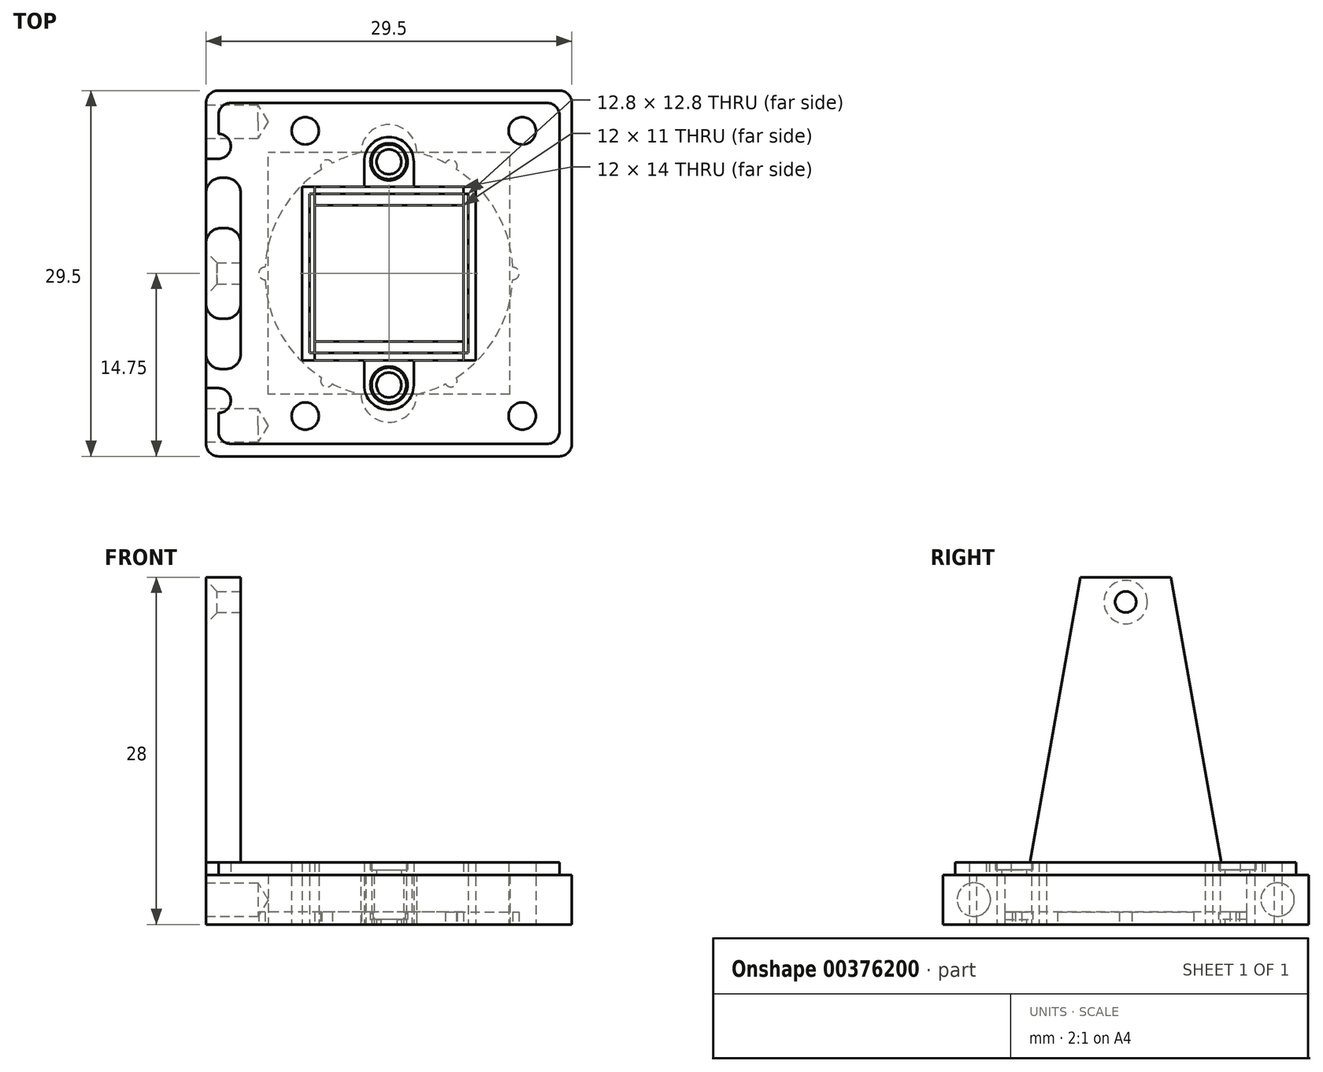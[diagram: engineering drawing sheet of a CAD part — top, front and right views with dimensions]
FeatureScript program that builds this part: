
annotation { "Feature Type Name" : "Feature", "Feature Type Description" : "" }
export const myFeature = defineFeature(function(context is Context, id is Id, definition is map)
    precondition{}
    {
        {
            var Q0;
            Q0=qCreatedBy(makeId("Top.planeOp"),FACE);
            var sketch = newSketch(context, id + "F0", { "sketchPlane" : qUnion([Q0])});
            skLineSegment(sketch, "E0.bottom", {"start": v(14.75, -14.75) * mm, "end": v(-14.75, -14.75) * mm});
            skLineSegment(sketch, "E0.top", {"start": v(14.75, 14.75) * mm, "end": v(-14.75, 14.75) * mm});
            skLineSegment(sketch, "E0.left", {"start": v(14.75, -14.75) * mm, "end": v(14.75, 14.75) * mm});
            skLineSegment(sketch, "E0.right", {"start": v(-14.75, -14.75) * mm, "end": v(-14.75, 14.75) * mm});
            skPoint(sketch, "E0.middle", {"position": v(0, 0) * mm});
            skLineSegment(sketch, "E1.0", {"start": v(-9.75, -9.75) * mm, "end": v(-9.75, 9.75) * mm});
            skLineSegment(sketch, "E1.1", {"start": v(9.75, -9.75) * mm, "end": v(-9.75, -9.75) * mm});
            skLineSegment(sketch, "E1.2", {"start": v(9.75, -9.75) * mm, "end": v(9.75, 9.75) * mm});
            skLineSegment(sketch, "E1.3", {"start": v(9.75, 9.75) * mm, "end": v(-9.75, 9.75) * mm});
            skSolve(sketch);
        }
        {
            var Q0;
            Q0 = qSketchRegion(id + "F0", true);
            extrude(context, id + "F1", {"entities" : qUnion([Q0]), "depth" : 4 * mm, "offsetDistance" : 25 * mm});
        }
        {
            var Q0;
            Q0=makeQuery(id+"F1.opExtrude","CAP_FACE",FACE,{"disambiguationData":[OSD([sQuery(id+"F0.wireOp",EDGE,"E0.bottom"),sQuery(id+"F0.wireOp",EDGE,"E0.top"),sQuery(id+"F0.wireOp",EDGE,"E0.left"),sQuery(id+"F0.wireOp",EDGE,"E0.right"),sQuery(id+"F0.wireOp",EDGE,"E1.0"),sQuery(id+"F0.wireOp",EDGE,"E1.1"),sQuery(id+"F0.wireOp",EDGE,"E1.2"),sQuery(id+"F0.wireOp",EDGE,"E1.3")])],"isStart":false});
            var sketch = newSketch(context, id + "F2", { "sketchPlane" : qUnion([Q0])});
            skLineSegment(sketch, "E2.0", {"start": v(13.75, 13.75) * mm, "end": v(-13.75, 13.75) * mm});
            skLineSegment(sketch, "E2.1", {"start": v(13.75, -13.75) * mm, "end": v(13.75, 13.75) * mm});
            skLineSegment(sketch, "E2.2", {"start": v(13.75, -13.75) * mm, "end": v(-13.75, -13.75) * mm});
            skLineSegment(sketch, "E2.3", {"start": v(-13.75, -13.75) * mm, "end": v(-13.75, -11.25) * mm});
            skLineSegment(sketch, "E3.bottom", {"start": v(-14.75, -8.65) * mm, "end": v(-11.95, -8.65) * mm});
            skLineSegment(sketch, "E3.top", {"start": v(-14.75, 8.65) * mm, "end": v(-11.95, 8.65) * mm});
            skLineSegment(sketch, "E3.left", {"start": v(-14.75, -8.65) * mm, "end": v(-14.75, 8.65) * mm});
            skLineSegment(sketch, "E3.right", {"start": v(-11.95, -8.65) * mm, "end": v(-11.95, 8.65) * mm});
            skPoint(sketch, "E3.middle", {"position": v(-13.35, 0) * mm});
            skPoint(sketch, "E3.middle.positionSnap0", {"position": v(-13.75, 0) * mm});
            skPoint(sketch, "E3.centerSnap0", {"position": v(-13.75, 0) * mm});
            skLineSegment(sketch, "E4.trimOffspring", {"start": v(-13.75, 11.25) * mm, "end": v(-13.75, 13.75) * mm});
            skArc(sketch, "E5", {"start": v(-13.75, 9.25) * mm, "mid": v(-12.75, 10.25) * mm, "end": v(-13.75, 11.25) * mm});
            skArc(sketch, "E6", {"start": v(-13.75, -11.25) * mm, "mid": v(-12.75, -10.25) * mm, "end": v(-13.75, -9.25) * mm});
            skLineSegment(sketch, "E7", {"start": v(-13.75, -9.25) * mm, "end": v(-14.75, -9.25) * mm});
            skLineSegment(sketch, "E8", {"start": v(-13.75, 9.25) * mm, "end": v(-14.75, 9.25) * mm});
            skCircle(sketch, "E9", {"center": v(0, 9.75) * mm, "radius": 2.25 * mm});
            skCircle(sketch, "E10", {"center": v(0, -9.75) * mm, "radius": 2.25 * mm});
            skCircle(sketch, "E11", {"center": v(0, 9.75) * mm, "radius": 1.25 * mm, "construction": true});
            skCircle(sketch, "E12", {"center": v(0, -9.75) * mm, "radius": 1.25 * mm, "construction": true});
            skLineSegment(sketch, "E13", {"start": v(-13.35, 0) * mm, "end": v(0, 0) * mm, "construction": true});
            skLineSegment(sketch, "E14.bottom", {"start": v(6, -7) * mm, "end": v(-6, -7) * mm});
            skLineSegment(sketch, "E14.top", {"start": v(6, 7) * mm, "end": v(-6, 7) * mm});
            skLineSegment(sketch, "E14.left", {"start": v(6, -7) * mm, "end": v(6, 7) * mm});
            skLineSegment(sketch, "E14.right", {"start": v(-6, -7) * mm, "end": v(-6, 7) * mm});
            skPoint(sketch, "E14.middle", {"position": v(0, 0) * mm});
            skSolve(sketch);
        }
        {
            var Q0;
            {var subQ5=sQuery(id+"F2.wireOp",EDGE,"E3.left");Q0=makeQuery(id+"F2.imprint","IMPRINT",FACE,{"disambiguationData":[TD([[makeQuery(id+"F2.imprint","IMPRINT",EDGE,{"derivedFrom":subQ5}),-1.0]])]});}
            var Q1;
            {var subQ5=sQuery(id+"F2.wireOp",EDGE,"E3.right");Q1=makeQuery(id+"F2.imprint","IMPRINT",FACE,{"disambiguationData":[TD([[makeQuery(id+"F2.imprint","IMPRINT",EDGE,{"derivedFrom":subQ5}),1.0]])]});}
            extrude(context, id + "F3", {"entities" : qUnion([Q0, Q1]), "operationType" : NewBodyOperationType.ADD, "depth" : 24 * mm, "offsetDistance" : 25 * mm});
        }
        {
            var Q0;
            Q0=makeQuery(id+"F3.opExtrude","CAP_EDGE",EDGE,{"disambiguationData":[OSD([sQuery(id+"F2.wireOp",EDGE,"E3.bottom")])],"isStart":false});
            var Q1;
            Q1=makeQuery(id+"F3.opExtrude","CAP_EDGE",EDGE,{"disambiguationData":[OSD([sQuery(id+"F2.wireOp",EDGE,"E3.top")])],"isStart":false});
            chamfer(context, id + "F4", {"entities" : qUnion([Q0, Q1]), "chamferType" : ChamferType.OFFSET_ANGLE, "width" : 5 * mm, "oppositeDirection" : false, "angle" : 80 * degree, "tangentPropagation" : true});
        }
        {
            var Q0;
            Q0=makeQuery(id+"F4.opChamfer","BLEND_EDGE",EDGE,{"blendedFrom":[makeQuery(id+"F3.opExtrude","CAP_EDGE",EDGE,{"disambiguationData":[OSD([sQuery(id+"F2.wireOp",EDGE,"E3.bottom")])],"isStart":false}),makeQuery(id+"F3.opExtrude","SWEPT_FACE",FACE,{"disambiguationData":[OSD([sQuery(id+"F2.wireOp",EDGE,"E3.right")])]})],"blendedInto":[makeQuery(id+"F3.opExtrude","SWEPT_FACE",FACE,{"disambiguationData":[OSD([sQuery(id+"F2.wireOp",EDGE,"E3.right")])]})]});
            var Q1;
            Q1=makeQuery(id+"F4.opChamfer","BLEND_EDGE",EDGE,{"blendedFrom":[makeQuery(id+"F3.opExtrude","CAP_EDGE",EDGE,{"disambiguationData":[OSD([sQuery(id+"F2.wireOp",EDGE,"E3.bottom")])],"isStart":false}),makeQuery(id+"F3.boolean.opBoolean","MERGE",FACE,{"derivedFrom":[makeQuery(id+"F1.opExtrude","SWEPT_FACE",FACE,{"disambiguationData":[OSD([sQuery(id+"F0.wireOp",EDGE,"E0.right")])]}),makeQuery(id+"F3.opExtrude","SWEPT_FACE",FACE,{"disambiguationData":[OSD([sQuery(id+"F2.wireOp",EDGE,"E3.left")])]})]})],"blendedInto":[makeQuery(id+"F3.boolean.opBoolean","MERGE",FACE,{"derivedFrom":[makeQuery(id+"F1.opExtrude","SWEPT_FACE",FACE,{"disambiguationData":[OSD([sQuery(id+"F0.wireOp",EDGE,"E0.right")])]}),makeQuery(id+"F3.opExtrude","SWEPT_FACE",FACE,{"disambiguationData":[OSD([sQuery(id+"F2.wireOp",EDGE,"E3.left")])]})]})]});
            var Q2;
            Q2=makeQuery(id+"F4.opChamfer","BLEND_EDGE",EDGE,{"blendedFrom":[makeQuery(id+"F3.opExtrude","CAP_EDGE",EDGE,{"disambiguationData":[OSD([sQuery(id+"F2.wireOp",EDGE,"E3.top")])],"isStart":false}),makeQuery(id+"F3.opExtrude","SWEPT_FACE",FACE,{"disambiguationData":[OSD([sQuery(id+"F2.wireOp",EDGE,"E3.right")])]})],"blendedInto":[makeQuery(id+"F3.opExtrude","SWEPT_FACE",FACE,{"disambiguationData":[OSD([sQuery(id+"F2.wireOp",EDGE,"E3.right")])]})]});
            var Q3;
            Q3=makeQuery(id+"F4.opChamfer","BLEND_EDGE",EDGE,{"blendedFrom":[makeQuery(id+"F3.opExtrude","CAP_EDGE",EDGE,{"disambiguationData":[OSD([sQuery(id+"F2.wireOp",EDGE,"E3.top")])],"isStart":false}),makeQuery(id+"F3.boolean.opBoolean","MERGE",FACE,{"derivedFrom":[makeQuery(id+"F1.opExtrude","SWEPT_FACE",FACE,{"disambiguationData":[OSD([sQuery(id+"F0.wireOp",EDGE,"E0.right")])]}),makeQuery(id+"F3.opExtrude","SWEPT_FACE",FACE,{"disambiguationData":[OSD([sQuery(id+"F2.wireOp",EDGE,"E3.left")])]})]})],"blendedInto":[makeQuery(id+"F3.boolean.opBoolean","MERGE",FACE,{"derivedFrom":[makeQuery(id+"F1.opExtrude","SWEPT_FACE",FACE,{"disambiguationData":[OSD([sQuery(id+"F0.wireOp",EDGE,"E0.right")])]}),makeQuery(id+"F3.opExtrude","SWEPT_FACE",FACE,{"disambiguationData":[OSD([sQuery(id+"F2.wireOp",EDGE,"E3.left")])]})]})]});
            fillet(context, id + "F5", {"entities" : qUnion([Q0, Q1, Q2, Q3]), "radius" : 1.2 * mm, "tangentPropagation" : true, "allowEdgeOverflow" : false});
        }
        {
            var Q0;
            {var subQ5=sQuery(id+"F2.wireOp",EDGE,"E8");Q0=makeQuery(id+"F2.imprint","IMPRINT",FACE,{"disambiguationData":[TD([[makeQuery(id+"F2.imprint","IMPRINT",EDGE,{"derivedFrom":subQ5}),1.0]])]});}
            var Q1;
            {var subQ8=sQuery(id+"F2.wireOp",EDGE,"E2.0");Q1=makeQuery(id+"F2.imprint","IMPRINT",FACE,{"disambiguationData":[TD([[makeQuery(id+"F2.imprint","IMPRINT",EDGE,{"derivedFrom":subQ8}),1.0]])]});}
            var Q2;
            {var subQ3=sQuery(id+"F2.wireOp",EDGE,"E7");Q2=makeQuery(id+"F2.imprint","IMPRINT",FACE,{"disambiguationData":[TD([[makeQuery(id+"F2.imprint","IMPRINT",EDGE,{"derivedFrom":subQ3}),-1.0]])]});}
            var Q3;
            {var subQ3=sQuery(id+"F2.wireOp",EDGE,"E3.left");Q3=makeQuery(id+"F2.imprint","IMPRINT",FACE,{"disambiguationData":[TD([[makeQuery(id+"F2.imprint","IMPRINT",EDGE,{"derivedFrom":subQ3}),-1.0]])]});}
            var Q4;
            Q4=makeQuery(id+"F2.imprint","IMPRINT",FACE,{"disambiguationData":[TD([[makeQuery(id+"F2.imprint","IMPRINT",EDGE,{"derivedFrom":sQuery(id+"F2.wireOp",EDGE,"E14.bottom")}),1.0]])]});
            var Q5;
            {var subQ0=sQuery(id+"F2.wireOp",EDGE,"E9");var subQ1=makeQuery(id+"F1.opExtrude","CAP_EDGE",EDGE,{"disambiguationData":[OSD([sQuery(id+"F0.wireOp",EDGE,"E1.3")])],"isStart":false});var subQ2=makeQuery(id+"F2.imprint","INTERSECT",VERTEX,{"disambiguationData":[OD(0.0)],"derivedFrom":[subQ1,subQ0]});Q5=makeQuery(id+"F2.imprint","IMPRINT",FACE,{"disambiguationData":[TD([[makeQuery(id+"F2.imprint","IMPRINT",EDGE,{"disambiguationData":[TD([[subQ2,-1.0]])],"derivedFrom":subQ0}),1.0]])]});}
            var Q6;
            {var subQ0=sQuery(id+"F2.wireOp",EDGE,"E9");var subQ1=makeQuery(id+"F1.opExtrude","CAP_EDGE",EDGE,{"disambiguationData":[OSD([sQuery(id+"F0.wireOp",EDGE,"E1.3")])],"isStart":false});var subQ2=makeQuery(id+"F2.imprint","INTERSECT",VERTEX,{"disambiguationData":[OD(0.0)],"derivedFrom":[subQ1,subQ0]});Q6=makeQuery(id+"F2.imprint","IMPRINT",FACE,{"disambiguationData":[TD([[makeQuery(id+"F2.imprint","IMPRINT",EDGE,{"disambiguationData":[TD([[subQ2,1.0]])],"derivedFrom":subQ0}),1.0]])]});}
            var Q7;
            {var subQ0=sQuery(id+"F2.wireOp",EDGE,"E10");var subQ1=makeQuery(id+"F1.opExtrude","CAP_EDGE",EDGE,{"disambiguationData":[OSD([sQuery(id+"F0.wireOp",EDGE,"E1.1")])],"isStart":false});var subQ2=makeQuery(id+"F2.imprint","INTERSECT",VERTEX,{"disambiguationData":[OD(0.0)],"derivedFrom":[subQ1,subQ0]});Q7=makeQuery(id+"F2.imprint","IMPRINT",FACE,{"disambiguationData":[TD([[makeQuery(id+"F2.imprint","IMPRINT",EDGE,{"disambiguationData":[TD([[subQ2,-1.0]])],"derivedFrom":subQ0}),1.0]])]});}
            var Q8;
            {var subQ0=sQuery(id+"F2.wireOp",EDGE,"E10");var subQ1=makeQuery(id+"F1.opExtrude","CAP_EDGE",EDGE,{"disambiguationData":[OSD([sQuery(id+"F0.wireOp",EDGE,"E1.1")])],"isStart":false});var subQ2=makeQuery(id+"F2.imprint","INTERSECT",VERTEX,{"disambiguationData":[OD(0.0)],"derivedFrom":[subQ1,subQ0]});Q8=makeQuery(id+"F2.imprint","IMPRINT",FACE,{"disambiguationData":[TD([[makeQuery(id+"F2.imprint","IMPRINT",EDGE,{"disambiguationData":[TD([[subQ2,1.0]])],"derivedFrom":subQ0}),1.0]])]});}
            var Q9;
            {var subQ0=sQuery(id+"F2.wireOp",EDGE,"E12");var subQ1=makeQuery(id+"F1.opExtrude","CAP_EDGE",EDGE,{"disambiguationData":[OSD([sQuery(id+"F0.wireOp",EDGE,"E1.1")])],"isStart":false});var subQ2=makeQuery(id+"F2.imprint","INTERSECT",VERTEX,{"disambiguationData":[OD(0.0)],"derivedFrom":[subQ1,subQ0]});Q9=makeQuery(id+"F2.imprint","IMPRINT",FACE,{"disambiguationData":[TD([[makeQuery(id+"F2.imprint","IMPRINT",EDGE,{"disambiguationData":[TD([[subQ2,-1.0]])],"derivedFrom":subQ0}),1.0]])]});}
            var Q10;
            {var subQ0=sQuery(id+"F2.wireOp",EDGE,"E11");var subQ1=makeQuery(id+"F1.opExtrude","CAP_EDGE",EDGE,{"disambiguationData":[OSD([sQuery(id+"F0.wireOp",EDGE,"E1.3")])],"isStart":false});var subQ2=makeQuery(id+"F2.imprint","INTERSECT",VERTEX,{"disambiguationData":[OD(0.0)],"derivedFrom":[subQ1,subQ0]});Q10=makeQuery(id+"F2.imprint","IMPRINT",FACE,{"disambiguationData":[TD([[makeQuery(id+"F2.imprint","IMPRINT",EDGE,{"disambiguationData":[TD([[subQ2,-1.0]])],"derivedFrom":subQ0}),1.0]])]});}
            var Q11;
            {var subQ0=sQuery(id+"F2.wireOp",EDGE,"E11");var subQ1=makeQuery(id+"F1.opExtrude","CAP_EDGE",EDGE,{"disambiguationData":[OSD([sQuery(id+"F0.wireOp",EDGE,"E1.3")])],"isStart":false});var subQ2=makeQuery(id+"F2.imprint","INTERSECT",VERTEX,{"disambiguationData":[OD(0.0)],"derivedFrom":[subQ1,subQ0]});Q11=makeQuery(id+"F2.imprint","IMPRINT",FACE,{"disambiguationData":[TD([[makeQuery(id+"F2.imprint","IMPRINT",EDGE,{"disambiguationData":[TD([[subQ2,1.0]])],"derivedFrom":subQ0}),1.0]])]});}
            var Q12;
            {var subQ0=sQuery(id+"F2.wireOp",EDGE,"E12");var subQ1=makeQuery(id+"F1.opExtrude","CAP_EDGE",EDGE,{"disambiguationData":[OSD([sQuery(id+"F0.wireOp",EDGE,"E1.1")])],"isStart":false});var subQ2=makeQuery(id+"F2.imprint","INTERSECT",VERTEX,{"disambiguationData":[OD(0.0)],"derivedFrom":[subQ1,subQ0]});Q12=makeQuery(id+"F2.imprint","IMPRINT",FACE,{"disambiguationData":[TD([[makeQuery(id+"F2.imprint","IMPRINT",EDGE,{"disambiguationData":[TD([[subQ2,1.0]])],"derivedFrom":subQ0}),1.0]])]});}
            extrude(context, id + "F6", {"entities" : qUnion([Q0, Q1, Q2, Q3, Q4, Q5, Q6, Q7, Q8, Q9, Q10, Q11, Q12]), "operationType" : NewBodyOperationType.ADD, "depth" : 1 * mm, "offsetDistance" : 25 * mm});
        }
        {
            var Q0;
            Q0=makeQuery(id+"F6.opExtrude","CAP_FACE",FACE,{"disambiguationData":[OSD([sQuery(id+"F0.wireOp",EDGE,"E0.right"),sQuery(id+"F0.wireOp",EDGE,"E1.0"),sQuery(id+"F0.wireOp",EDGE,"E1.1"),sQuery(id+"F0.wireOp",EDGE,"E1.2"),sQuery(id+"F0.wireOp",EDGE,"E1.3"),sQuery(id+"F2.wireOp",EDGE,"E2.0"),sQuery(id+"F2.wireOp",EDGE,"E2.1"),sQuery(id+"F2.wireOp",EDGE,"E2.2"),sQuery(id+"F2.wireOp",EDGE,"E2.3"),sQuery(id+"F2.wireOp",EDGE,"E3.left"),sQuery(id+"F2.wireOp",EDGE,"E4.trimOffspring"),sQuery(id+"F2.wireOp",EDGE,"E5"),sQuery(id+"F2.wireOp",EDGE,"E6"),sQuery(id+"F2.wireOp",EDGE,"E7"),sQuery(id+"F2.wireOp",EDGE,"E8"),sQuery(id+"F2.wireOp",EDGE,"E9"),sQuery(id+"F2.wireOp",EDGE,"E10")])],"isStart":false});
            var sketch = newSketch(context, id + "F7", { "sketchPlane" : qUnion([Q0])});
            skCircle(sketch, "E15", {"center": v(10.75, 11.5) * mm, "radius": 1.19 * mm});
            skCircle(sketch, "E16", {"center": v(10.75, -11.5) * mm, "radius": 1.19 * mm});
            skCircle(sketch, "E17", {"center": v(-6.75, 11.5) * mm, "radius": 1.4 * mm});
            skCircle(sketch, "E18", {"center": v(-6.75, -11.5) * mm, "radius": 1.2 * mm});
            skLineSegment(sketch, "E19", {"start": v(0, 0) * mm, "end": v(6.78, 0) * mm, "construction": true});
            skCircle(sketch, "E20", {"center": v(0, -9) * mm, "radius": 0.9 * mm});
            skCircle(sketch, "E21", {"center": v(0, 9) * mm, "radius": 2.16 * mm});
            skSolve(sketch);
        }
        {
            var Q0;
            Q0=sQuery(id+"F7.wireOp",VERTEX,"E15.center");
            var Q1;
            Q1=sQuery(id+"F7.wireOp",VERTEX,"E16.center");
            var Q2;
            Q2=sQuery(id+"F7.wireOp",VERTEX,"E17.center");
            var Q3;
            Q3=sQuery(id+"F7.wireOp",VERTEX,"E18.center");
            var Q4;
            Q4=makeQuery(id+"F1.opExtrude","SWEPT_BODY",BODY,{"disambiguationData":[OSD([sQuery(id+"F0.wireOp",EDGE,"E0.bottom"),sQuery(id+"F0.wireOp",EDGE,"E0.top"),sQuery(id+"F0.wireOp",EDGE,"E0.left"),sQuery(id+"F0.wireOp",EDGE,"E0.right"),sQuery(id+"F0.wireOp",EDGE,"E1.0"),sQuery(id+"F0.wireOp",EDGE,"E1.1"),sQuery(id+"F0.wireOp",EDGE,"E1.2"),sQuery(id+"F0.wireOp",EDGE,"E1.3")])]});
            hole(context, id + "F8", {"style" : HoleStyle.SIMPLE, "endStyle" : HoleEndStyle.BLIND, "holeDiameter" : 2.2 * mm, "majorDiameter" : 5 * mm, "holeDepth" : 20 * mm, "isTappedThrough" : true, "tappedDepth" : 12 * mm, "tapClearance" : 3, "locations" : qUnion([Q0, Q1, Q2, Q3]), "scope" : qUnion([Q4])});
        }
        {
            var Q0;
            Q0=qCreatedBy(makeId("Top.planeOp"),FACE);
            var sketch = newSketch(context, id + "F9", { "sketchPlane" : qUnion([Q0])});
            skCircle(sketch, "E22", {"center": v(0, 0) * mm, "radius": 10 * mm});
            skLineSegment(sketch, "E23.bottom", {"start": v(6, -5.5) * mm, "end": v(-6, -5.5) * mm});
            skLineSegment(sketch, "E23.top", {"start": v(6, 5.5) * mm, "end": v(-6, 5.5) * mm});
            skLineSegment(sketch, "E23.left", {"start": v(6, -5.5) * mm, "end": v(6, 5.5) * mm});
            skLineSegment(sketch, "E23.right", {"start": v(-6, -5.5) * mm, "end": v(-6, 5.5) * mm});
            skCircle(sketch, "E24", {"center": v(0, 10) * mm, "radius": 2 * mm});
            skCircle(sketch, "E25", {"center": v(0, -10) * mm, "radius": 2 * mm});
            skCircle(sketch, "E26", {"center": v(10, 0) * mm, "radius": 0.5 * mm});
            skCircle(sketch, "E27.1.0", {"center": v(5, 8.66) * mm, "radius": 0.5 * mm});
            skCircle(sketch, "E27.2.0", {"center": v(-5, 8.66) * mm, "radius": 0.5 * mm});
            skCircle(sketch, "E28.1.3.0", {"center": v(-10, 0) * mm, "radius": 0.5 * mm});
            skCircle(sketch, "E28.1.4.0", {"center": v(-5, -8.66) * mm, "radius": 0.5 * mm});
            skCircle(sketch, "E28.1.5.0", {"center": v(5, -8.66) * mm, "radius": 0.5 * mm});
            skSolve(sketch);
        }
        {
            var Q0;
            Q0 = qSketchRegion(id + "F9", true);
            var Q1;
            {var subQ0=sQuery(id+"F9.wireOp",EDGE,"nrrdsNW8-0lje-5FPb-w1w5-OaGebltPMd51");var subQ1=sQuery(id+"F9.wireOp",EDGE,"E22");var subQ2=makeQuery(id+"F9.imprint","INTERSECT",VERTEX,{"disambiguationData":[OD(0.0)],"derivedFrom":[subQ1,subQ0]});Q1=makeQuery(id+"F9.imprint","IMPRINT",FACE,{"disambiguationData":[TD([[makeQuery(id+"F9.imprint","IMPRINT",EDGE,{"disambiguationData":[TD([[subQ2,-1.0]])],"derivedFrom":subQ1}),1.0]])]});}
            var Q2;
            {var subQ0=sQuery(id+"F9.wireOp",EDGE,"nrrdsNW8-0lje-5FPb-w1w5-OaGebltPMd51");var subQ1=sQuery(id+"F9.wireOp",EDGE,"E22");var subQ2=makeQuery(id+"F9.imprint","INTERSECT",VERTEX,{"disambiguationData":[OD(0.0)],"derivedFrom":[subQ1,subQ0]});Q2=makeQuery(id+"F9.imprint","IMPRINT",FACE,{"disambiguationData":[TD([[makeQuery(id+"F9.imprint","IMPRINT",EDGE,{"disambiguationData":[TD([[subQ2,-1.0]])],"derivedFrom":subQ1}),-1.0]])]});}
            var Q3;
            {var subQ0=sQuery(id+"F9.wireOp",EDGE,"nrrdsNW8-0lje-5FPb-w1w5-OaGebltPMd51");var subQ1=sQuery(id+"F9.wireOp",EDGE,"E24");var subQ2=makeQuery(id+"F9.imprint","INTERSECT",VERTEX,{"disambiguationData":[OD(0.0)],"derivedFrom":[subQ1,subQ0]});Q3=makeQuery(id+"F9.imprint","IMPRINT",FACE,{"disambiguationData":[TD([[makeQuery(id+"F9.imprint","IMPRINT",EDGE,{"disambiguationData":[TD([[subQ2,-1.0]])],"derivedFrom":subQ1}),-1.0]])]});}
            var Q4;
            {var subQ0=sQuery(id+"F9.wireOp",EDGE,"S1DDepDF-IZdj-yKmF-IfUE-yXN7PUjpcanx");var subQ1=sQuery(id+"F9.wireOp",EDGE,"E22");var subQ2=makeQuery(id+"F9.imprint","INTERSECT",VERTEX,{"disambiguationData":[OD(0.0)],"derivedFrom":[subQ1,subQ0]});Q4=makeQuery(id+"F9.imprint","IMPRINT",FACE,{"disambiguationData":[TD([[makeQuery(id+"F9.imprint","IMPRINT",EDGE,{"disambiguationData":[TD([[subQ2,-1.0]])],"derivedFrom":subQ1}),1.0]])]});}
            var Q5;
            {var subQ0=sQuery(id+"F9.wireOp",EDGE,"S1DDepDF-IZdj-yKmF-IfUE-yXN7PUjpcanx");var subQ1=sQuery(id+"F9.wireOp",EDGE,"E25");var subQ2=makeQuery(id+"F9.imprint","INTERSECT",VERTEX,{"disambiguationData":[OD(0.0)],"derivedFrom":[subQ1,subQ0]});Q5=makeQuery(id+"F9.imprint","IMPRINT",FACE,{"disambiguationData":[TD([[makeQuery(id+"F9.imprint","IMPRINT",EDGE,{"disambiguationData":[TD([[subQ2,-1.0]])],"derivedFrom":subQ1}),-1.0]])]});}
            var Q6;
            {var subQ0=sQuery(id+"F9.wireOp",EDGE,"S1DDepDF-IZdj-yKmF-IfUE-yXN7PUjpcanx");var subQ1=sQuery(id+"F9.wireOp",EDGE,"E22");var subQ2=makeQuery(id+"F9.imprint","INTERSECT",VERTEX,{"disambiguationData":[OD(0.0)],"derivedFrom":[subQ1,subQ0]});Q6=makeQuery(id+"F9.imprint","IMPRINT",FACE,{"disambiguationData":[TD([[makeQuery(id+"F9.imprint","IMPRINT",EDGE,{"disambiguationData":[TD([[subQ2,-1.0]])],"derivedFrom":subQ1}),-1.0]])]});}
            extrude(context, id + "F10", {"entities" : qUnion([Q0, Q1, Q2, Q3, Q4, Q5, Q6]), "depth" : 1 * mm, "offsetDistance" : 25 * mm});
        }
        {
            var Q0;
            Q0=qCreatedBy(makeId("Top.planeOp"),FACE);
            var sketch = newSketch(context, id + "F11", { "sketchPlane" : qUnion([Q0])});
            skLineSegment(sketch, "E29.bottom", {"start": v(7, -7) * mm, "end": v(-7, -7) * mm});
            skLineSegment(sketch, "E29.top", {"start": v(7, 7) * mm, "end": v(-7, 7) * mm});
            skLineSegment(sketch, "E29.left", {"start": v(7, -7) * mm, "end": v(7, 7) * mm});
            skLineSegment(sketch, "E29.right", {"start": v(-7, -7) * mm, "end": v(-7, 7) * mm});
            skPoint(sketch, "E29.middle", {"position": v(0, 0) * mm});
            skLineSegment(sketch, "E30.0", {"start": v(6.4, 6.4) * mm, "end": v(-6.4, 6.4) * mm});
            skLineSegment(sketch, "E30.1", {"start": v(6.4, -6.4) * mm, "end": v(6.4, 6.4) * mm});
            skLineSegment(sketch, "E30.2", {"start": v(6.4, -6.4) * mm, "end": v(-6.4, -6.4) * mm});
            skLineSegment(sketch, "E30.3", {"start": v(-6.4, -6.4) * mm, "end": v(-6.4, 6.4) * mm});
            skCircle(sketch, "E31", {"center": v(0, 9) * mm, "radius": 2 * mm});
            skPoint(sketch, "E31.centerSnap0", {"position": v(0, 7) * mm});
            skCircle(sketch, "E32.0", {"center": v(0, 9) * mm, "radius": 1.4 * mm});
            skCircle(sketch, "E33", {"center": v(0, -9) * mm, "radius": 2 * mm});
            skPoint(sketch, "E33.centerSnap0", {"position": v(0, -7) * mm});
            skCircle(sketch, "E34.0", {"center": v(0, -9) * mm, "radius": 1.4 * mm});
            skLineSegment(sketch, "E35", {"start": v(-2.78, 9) * mm, "end": v(3.33, 9) * mm, "construction": true});
            skLineSegment(sketch, "E36", {"start": v(-2.82, -9) * mm, "end": v(3.88, -9) * mm, "construction": true});
            skLineSegment(sketch, "E37", {"start": v(-2, 9) * mm, "end": v(-2, 7) * mm});
            skLineSegment(sketch, "E38", {"start": v(2, 9) * mm, "end": v(2, 7) * mm});
            skLineSegment(sketch, "E39", {"start": v(-2, -9) * mm, "end": v(-2, -7) * mm});
            skLineSegment(sketch, "E40", {"start": v(2, -9) * mm, "end": v(2, -7) * mm});
            skSolve(sketch);
        }
        {
            var Q0;
            {var subQ0=sQuery(id+"F11.wireOp",EDGE,"E37");Q0=makeQuery(id+"F11.imprint","IMPRINT",FACE,{"disambiguationData":[TD([[makeQuery(id+"F11.imprint","IMPRINT",EDGE,{"derivedFrom":subQ0}),1.0]])]});}
            var Q1;
            Q1=makeQuery(id+"F11.imprint","IMPRINT",FACE,{"disambiguationData":[TD([[makeQuery(id+"F11.imprint","IMPRINT",EDGE,{"derivedFrom":sQuery(id+"F11.wireOp",EDGE,"E32.0")}),-1.0]])]});
            var Q2;
            {var subQ0=sQuery(id+"F11.wireOp",EDGE,"E38");Q2=makeQuery(id+"F11.imprint","IMPRINT",FACE,{"disambiguationData":[TD([[makeQuery(id+"F11.imprint","IMPRINT",EDGE,{"derivedFrom":subQ0}),-1.0]])]});}
            var Q3;
            {var subQ1=sQuery(id+"F11.wireOp",EDGE,"E29.left");Q3=makeQuery(id+"F11.imprint","IMPRINT",FACE,{"disambiguationData":[TD([[makeQuery(id+"F11.imprint","IMPRINT",EDGE,{"derivedFrom":subQ1}),1.0]])]});}
            var Q4;
            {var subQ0=sQuery(id+"F11.wireOp",EDGE,"E40");Q4=makeQuery(id+"F11.imprint","IMPRINT",FACE,{"disambiguationData":[TD([[makeQuery(id+"F11.imprint","IMPRINT",EDGE,{"derivedFrom":subQ0}),1.0]])]});}
            var Q5;
            Q5=makeQuery(id+"F11.imprint","IMPRINT",FACE,{"disambiguationData":[TD([[makeQuery(id+"F11.imprint","IMPRINT",EDGE,{"derivedFrom":sQuery(id+"F11.wireOp",EDGE,"E34.0")}),-1.0]])]});
            var Q6;
            {var subQ0=sQuery(id+"F11.wireOp",EDGE,"E39");Q6=makeQuery(id+"F11.imprint","IMPRINT",FACE,{"disambiguationData":[TD([[makeQuery(id+"F11.imprint","IMPRINT",EDGE,{"derivedFrom":subQ0}),-1.0]])]});}
            extrude(context, id + "F12", {"entities" : qUnion([Q0, Q1, Q2, Q3, Q4, Q5, Q6]), "depth" : 5 * mm, "offsetDistance" : 25 * mm});
        }
        {
            var Q0;
            {var subQ0=sQuery(id+"F2.wireOp",EDGE,"E3.left");var subQ1=sQuery(id+"F0.wireOp",EDGE,"E0.right");Q0=makeQuery(id+"F6.boolean.opBoolean","MERGE",FACE,{"derivedFrom":[makeQuery(id+"F3.boolean.opBoolean","MERGE",FACE,{"derivedFrom":[makeQuery(id+"F1.opExtrude","SWEPT_FACE",FACE,{"disambiguationData":[OSD([subQ1])]}),makeQuery(id+"F3.opExtrude","SWEPT_FACE",FACE,{"disambiguationData":[OSD([subQ0])]})]}),makeQuery(id+"F6.opExtrude","SWEPT_FACE",FACE,{"disambiguationData":[OSD([subQ1,subQ0])]})]});}
            var sketch = newSketch(context, id + "F13", { "sketchPlane" : qUnion([Q0])});
            skCircle(sketch, "E41", {"center": v(0, 26) * mm, "radius": 0.1 * mm});
            skCircle(sketch, "E42", {"center": v(-12.25, 2) * mm, "radius": 1.3 * mm});
            skPoint(sketch, "E42.centerSnap0", {"position": v(-14.75, 2) * mm});
            skCircle(sketch, "E43", {"center": v(12.25, 2) * mm, "radius": 1.3 * mm});
            skPoint(sketch, "E43.centerSnap0", {"position": v(14.75, 2) * mm});
            skSolve(sketch);
        }
        {
            var Q0;
            Q0=sQuery(id+"F13.wireOp",VERTEX,"E41.center");
            var Q1;
            Q1=makeQuery(id+"F1.opExtrude","SWEPT_BODY",BODY,{"disambiguationData":[OSD([sQuery(id+"F0.wireOp",EDGE,"E0.bottom"),sQuery(id+"F0.wireOp",EDGE,"E0.top"),sQuery(id+"F0.wireOp",EDGE,"E0.left"),sQuery(id+"F0.wireOp",EDGE,"E0.right"),sQuery(id+"F0.wireOp",EDGE,"E1.0"),sQuery(id+"F0.wireOp",EDGE,"E1.1"),sQuery(id+"F0.wireOp",EDGE,"E1.2"),sQuery(id+"F0.wireOp",EDGE,"E1.3")])]});
            hole(context, id + "F14", {"style" : HoleStyle.C_SINK, "endStyle" : HoleEndStyle.BLIND, "holeDiameter" : 1.7 * mm, "cSinkDiameter" : 3.5 * mm, "cSinkAngle" : 90 * degree, "majorDiameter" : 5 * mm, "holeDepth" : 5 * mm, "isTappedThrough" : true, "tappedDepth" : 12 * mm, "tapClearance" : 3, "locations" : qUnion([Q0]), "scope" : qUnion([Q1])});
        }
        {
            var Q0;
            Q0=sQuery(id+"F13.wireOp",VERTEX,"E42.center");
            var Q1;
            Q1=sQuery(id+"F13.wireOp",VERTEX,"E43.center");
            var Q2;
            Q2=makeQuery(id+"F1.opExtrude","SWEPT_BODY",BODY,{"disambiguationData":[OSD([sQuery(id+"F0.wireOp",EDGE,"E0.bottom"),sQuery(id+"F0.wireOp",EDGE,"E0.top"),sQuery(id+"F0.wireOp",EDGE,"E0.left"),sQuery(id+"F0.wireOp",EDGE,"E0.right"),sQuery(id+"F0.wireOp",EDGE,"E1.0"),sQuery(id+"F0.wireOp",EDGE,"E1.1"),sQuery(id+"F0.wireOp",EDGE,"E1.2"),sQuery(id+"F0.wireOp",EDGE,"E1.3")])]});
            hole(context, id + "F15", {"style" : HoleStyle.SIMPLE, "endStyle" : HoleEndStyle.BLIND, "holeDiameter" : 2.7 * mm, "majorDiameter" : 5 * mm, "holeDepth" : 4.2 * mm, "isTappedThrough" : true, "tappedDepth" : 12 * mm, "tapClearance" : 3, "locations" : qUnion([Q0, Q1]), "scope" : qUnion([Q2])});
        }
        {
            var Q0;
            Q0=makeQuery(id+"F10.opExtrude","CAP_FACE",FACE,{"disambiguationData":[OSD([sQuery(id+"F9.wireOp",EDGE,"E22"),sQuery(id+"F9.wireOp",EDGE,"E23.bottom"),sQuery(id+"F9.wireOp",EDGE,"E23.top"),sQuery(id+"F9.wireOp",EDGE,"E23.left"),sQuery(id+"F9.wireOp",EDGE,"E23.right"),sQuery(id+"F9.wireOp",EDGE,"E24"),sQuery(id+"F9.wireOp",EDGE,"E25"),sQuery(id+"F9.wireOp",EDGE,"E26"),sQuery(id+"F9.wireOp",EDGE,"E27.1.0"),sQuery(id+"F9.wireOp",EDGE,"E27.2.0"),sQuery(id+"F9.wireOp",EDGE,"E28.1.3.0"),sQuery(id+"F9.wireOp",EDGE,"E28.1.4.0"),sQuery(id+"F9.wireOp",EDGE,"E28.1.5.0")])],"isStart":false});
            var sketch = newSketch(context, id + "F16", { "sketchPlane" : qUnion([Q0])});
            skCircle(sketch, "E44", {"center": v(0, 9) * mm, "radius": 0.98 * mm});
            skCircle(sketch, "E45", {"center": v(0, -9) * mm, "radius": 1.12 * mm});
            skSolve(sketch);
        }
        {
            var Q0;
            Q0=sQuery(id+"F16.wireOp",VERTEX,"E44.center");
            var Q1;
            Q1=sQuery(id+"F16.wireOp",VERTEX,"E45.center");
            var Q2;
            Q2=makeQuery(id+"F10.opExtrude","SWEPT_BODY",BODY,{"disambiguationData":[OSD([sQuery(id+"F9.wireOp",EDGE,"E22"),sQuery(id+"F9.wireOp",EDGE,"E23.bottom"),sQuery(id+"F9.wireOp",EDGE,"E23.top"),sQuery(id+"F9.wireOp",EDGE,"E23.left"),sQuery(id+"F9.wireOp",EDGE,"E23.right"),sQuery(id+"F9.wireOp",EDGE,"E24"),sQuery(id+"F9.wireOp",EDGE,"E25"),sQuery(id+"F9.wireOp",EDGE,"E26"),sQuery(id+"F9.wireOp",EDGE,"E27.1.0"),sQuery(id+"F9.wireOp",EDGE,"E27.2.0"),sQuery(id+"F9.wireOp",EDGE,"E28.1.3.0"),sQuery(id+"F9.wireOp",EDGE,"E28.1.4.0"),sQuery(id+"F9.wireOp",EDGE,"E28.1.5.0")])]});
            hole(context, id + "F17", {"style" : HoleStyle.C_BORE, "endStyle" : HoleEndStyle.BLIND, "holeDiameter" : 2 * mm, "cBoreDiameter" : 3 * mm, "cBoreDepth" : 0.6 * mm, "majorDiameter" : 5 * mm, "holeDepth" : 4.2 * mm, "isTappedThrough" : true, "tappedDepth" : 12 * mm, "tapClearance" : 3, "locations" : qUnion([Q0, Q1]), "scope" : qUnion([Q2])});
        }
        {
            var Q0;
            Q0=sQuery(id+"F7.wireOp",VERTEX,"E21.center");
            var Q1;
            Q1=sQuery(id+"F7.wireOp",VERTEX,"E20.center");
            var Q2;
            Q2=makeQuery(id+"F1.opExtrude","SWEPT_BODY",BODY,{"disambiguationData":[OSD([sQuery(id+"F0.wireOp",EDGE,"E0.bottom"),sQuery(id+"F0.wireOp",EDGE,"E0.top"),sQuery(id+"F0.wireOp",EDGE,"E0.left"),sQuery(id+"F0.wireOp",EDGE,"E0.right"),sQuery(id+"F0.wireOp",EDGE,"E1.0"),sQuery(id+"F0.wireOp",EDGE,"E1.1"),sQuery(id+"F0.wireOp",EDGE,"E1.2"),sQuery(id+"F0.wireOp",EDGE,"E1.3")])]});
            hole(context, id + "F18", {"style" : HoleStyle.C_BORE, "endStyle" : HoleEndStyle.BLIND, "holeDiameter" : 2 * mm, "cBoreDiameter" : 3 * mm, "cBoreDepth" : 0.6 * mm, "majorDiameter" : 5 * mm, "holeDepth" : 20 * mm, "isTappedThrough" : true, "tappedDepth" : 12 * mm, "tapClearance" : 3, "locations" : qUnion([Q0, Q1]), "scope" : qUnion([Q2])});
        }
        {
            var Q0;
            {var subQ0=sQuery(id+"F2.wireOp",EDGE,"E9");var subQ1=makeQuery(id+"F1.opExtrude","CAP_EDGE",EDGE,{"disambiguationData":[OSD([sQuery(id+"F0.wireOp",EDGE,"E1.3")])],"isStart":false});var subQ2=makeQuery(id+"F2.imprint","INTERSECT",VERTEX,{"disambiguationData":[OD(0.0)],"derivedFrom":[subQ1,subQ0]});Q0=makeQuery(id+"F2.imprint","IMPRINT",FACE,{"disambiguationData":[TD([[makeQuery(id+"F2.imprint","IMPRINT",EDGE,{"disambiguationData":[TD([[subQ2,1.0]])],"derivedFrom":subQ0}),1.0]])]});}
            var Q1;
            {var subQ0=sQuery(id+"F2.wireOp",EDGE,"E10");var subQ1=makeQuery(id+"F1.opExtrude","CAP_EDGE",EDGE,{"disambiguationData":[OSD([sQuery(id+"F0.wireOp",EDGE,"E1.1")])],"isStart":false});var subQ2=makeQuery(id+"F2.imprint","INTERSECT",VERTEX,{"disambiguationData":[OD(0.0)],"derivedFrom":[subQ1,subQ0]});Q1=makeQuery(id+"F2.imprint","IMPRINT",FACE,{"disambiguationData":[TD([[makeQuery(id+"F2.imprint","IMPRINT",EDGE,{"disambiguationData":[TD([[subQ2,-1.0]])],"derivedFrom":subQ0}),1.0]])]});}
            extrude(context, id + "F19", {"entities" : qUnion([Q0, Q1]), "operationType" : NewBodyOperationType.REMOVE, "oppositeDirection" : true, "depth" : 25 * mm, "offsetDistance" : 25 * mm});
        }
        {
            var Q0;
            Q0=makeQuery(id+"F1.opExtrude","SWEPT_EDGE",EDGE,{"disambiguationData":[OSD([sQuery(id+"F0.wireOp",EDGE,"E0.bottom"),sQuery(id+"F0.wireOp",EDGE,"E0.right")])]});
            var Q1;
            Q1=makeQuery(id+"F6.opExtrude","SWEPT_EDGE",EDGE,{"disambiguationData":[OSD([sQuery(id+"F2.wireOp",EDGE,"E2.2"),sQuery(id+"F2.wireOp",EDGE,"E2.3")])]});
            var Q2;
            Q2=makeQuery(id+"F6.opExtrude","SWEPT_EDGE",EDGE,{"disambiguationData":[OSD([sQuery(id+"F2.wireOp",EDGE,"E2.1"),sQuery(id+"F2.wireOp",EDGE,"E2.2")])]});
            var Q3;
            Q3=makeQuery(id+"F1.opExtrude","SWEPT_EDGE",EDGE,{"disambiguationData":[OSD([sQuery(id+"F0.wireOp",EDGE,"E0.bottom"),sQuery(id+"F0.wireOp",EDGE,"E0.left")])]});
            var Q4;
            Q4=makeQuery(id+"F6.opExtrude","SWEPT_EDGE",EDGE,{"disambiguationData":[OSD([sQuery(id+"F2.wireOp",EDGE,"E2.0"),sQuery(id+"F2.wireOp",EDGE,"E2.1")])]});
            var Q5;
            Q5=makeQuery(id+"F1.opExtrude","SWEPT_EDGE",EDGE,{"disambiguationData":[OSD([sQuery(id+"F0.wireOp",EDGE,"E0.top"),sQuery(id+"F0.wireOp",EDGE,"E0.left")])]});
            var Q6;
            Q6=makeQuery(id+"F6.opExtrude","SWEPT_EDGE",EDGE,{"disambiguationData":[OSD([sQuery(id+"F2.wireOp",EDGE,"E2.0"),sQuery(id+"F2.wireOp",EDGE,"E4.trimOffspring")])]});
            var Q7;
            Q7=makeQuery(id+"F1.opExtrude","SWEPT_EDGE",EDGE,{"disambiguationData":[OSD([sQuery(id+"F0.wireOp",EDGE,"E0.top"),sQuery(id+"F0.wireOp",EDGE,"E0.right")])]});
            fillet(context, id + "F20", {"entities" : qUnion([Q0, Q1, Q2, Q3, Q4, Q5, Q6, Q7]), "radius" : 1 * mm, "tangentPropagation" : true, "allowEdgeOverflow" : false});
        }
    });
